# Revit family: Maxlogic siren,flaşör,flaşörlü siren (Düşük ıp)
name_source: partatom
category: Fire Alarm Devices
units: mm (PartAtom-declared; Revit-internal decimal feet)

## family parameters
Cut with Voids When Loaded = No
Host = Face
Maintain Annotation Orientation = Yes
OmniClass Number = 23.85.30.21
OmniClass Title = Environmental Detection/Registration
Part Type = Normal
Room Calculation Point = No
Round Connector Dimension = Use Diameter
Shared = No

## types (9) — shared parameters
Color = Kırmızı
Fax Number = (+)90 216 466 45 10
Installation Manual = https://mavilielektronik.com
Main Material = Red Plastic ABS
Manufacturer = Mavili Elektronik Ticaret A.Ş.
Model = MaxLogic
Mounting height = Zeminden 2,4 m yukarıda
Mounting surface = Duvara montaj
Nominal Height = 122 mm
Nominal Width = 122 mm
Operating temperature = (-10°C) - (+55°C)
Operatonal Voltage (default) = 24 V/DC
Protection Sign = IP21C
Secondary Material = Plastic
URL = https://www.mavili.com.tr
Warranty Duration Labor = 2
Warranty Duration Parts = 2
Warranty Duration Unit = Year
zero-valued in all types: Cost, Default Elevation

## per-type parameters (varying)
| type | Code Performance | Description | Device Adress Setup | Flaşör | Nominal Depth | Operating voltage range | Product Code | Public Works Pose Number | Weight |
| Maxlogic Konvansiyonel Elektronik Siren | EN 54-3 | Konvansiyonel Elektronik Siren |  | No | 90 mm | 21-28 V/DC | ML-2410 | 833-590 | 195 gr. |
| Maxlogic Konvansiyonel Flaşör | EN 54-23 | Konvansiyonel Flaşör |  | Yes | 101,5 mm | 21-28 V/DC | ML-2420 | 833-591 | 205 gr. |
| Maxlogic Konvansiyonel Flaşörlü Elektronik Siren | EN 54-3 / EN 54-23 | Konvansiyonel Flaşörlü Elektronik Siren |  | Yes | 101,5 mm | 21-28 V/DC | ML-2430 | 833-592 | 220 gr. |
| Maxlogic Adresli Elektronik Siren | EN 54-3 | Adresli Elektronik Siren | El tipi adresleme cihazı | No | 90 mm | 18-33 V/DC | ML-1410 |  | 186 gr. |
| Maxlogic Adresli Elektronik Siren, Kısa Devre İzolatörlü | EN 54-3 | Adresli Elektronik Siren kısa devre izolatörlü | El tipi adresleme cihazı | No | 90 mm | 18-33 V/DC | ML-1410.SCI |  | 186 gr. |
| Maxlogic Adresli Flaşör | EN 54-23 | Adresli Flaşör | El tipi adresleme cihazı | Yes | 90 mm | 18-33 V/DC | ML-1420 |  | 201 gr. |
| Maxlogic Adresli Flaşör, Kısa Devre İzolatörlü | EN 54-23 | Adresli Flaşör kısa devre izolatörlü | El tipi adresleme cihazı | Yes | 90 mm | 18-33 V/DC | ML-1420.SCI |  | 201 gr. |
| Maxlogic Adresli Flaşörlü Elektronik Siren | EN 54-3 / EN 54-23 | Adresli Flaşörlü Elektronik Siren | El tipi adresleme cihazı | Yes | 90 mm | 18-33 V/DC | ML-1430 |  | 217 gr. |
| Maxlogic Adresli Flaşörlü Elektronik Siren, Kısa Devre İzolatörlü | EN 54-3 / EN 54-23 | Adresli Flaşörlü Elektronik Siren kısa devre izolatörlü | El tipi adresleme cihazı | Yes | 90 mm | 18-33 V/DC | ML-1430.SCI |  | 217 gr. |

## geometry (parser evidence)
native form markers: Sweep x5
no freeform markers — native parametric forms only
